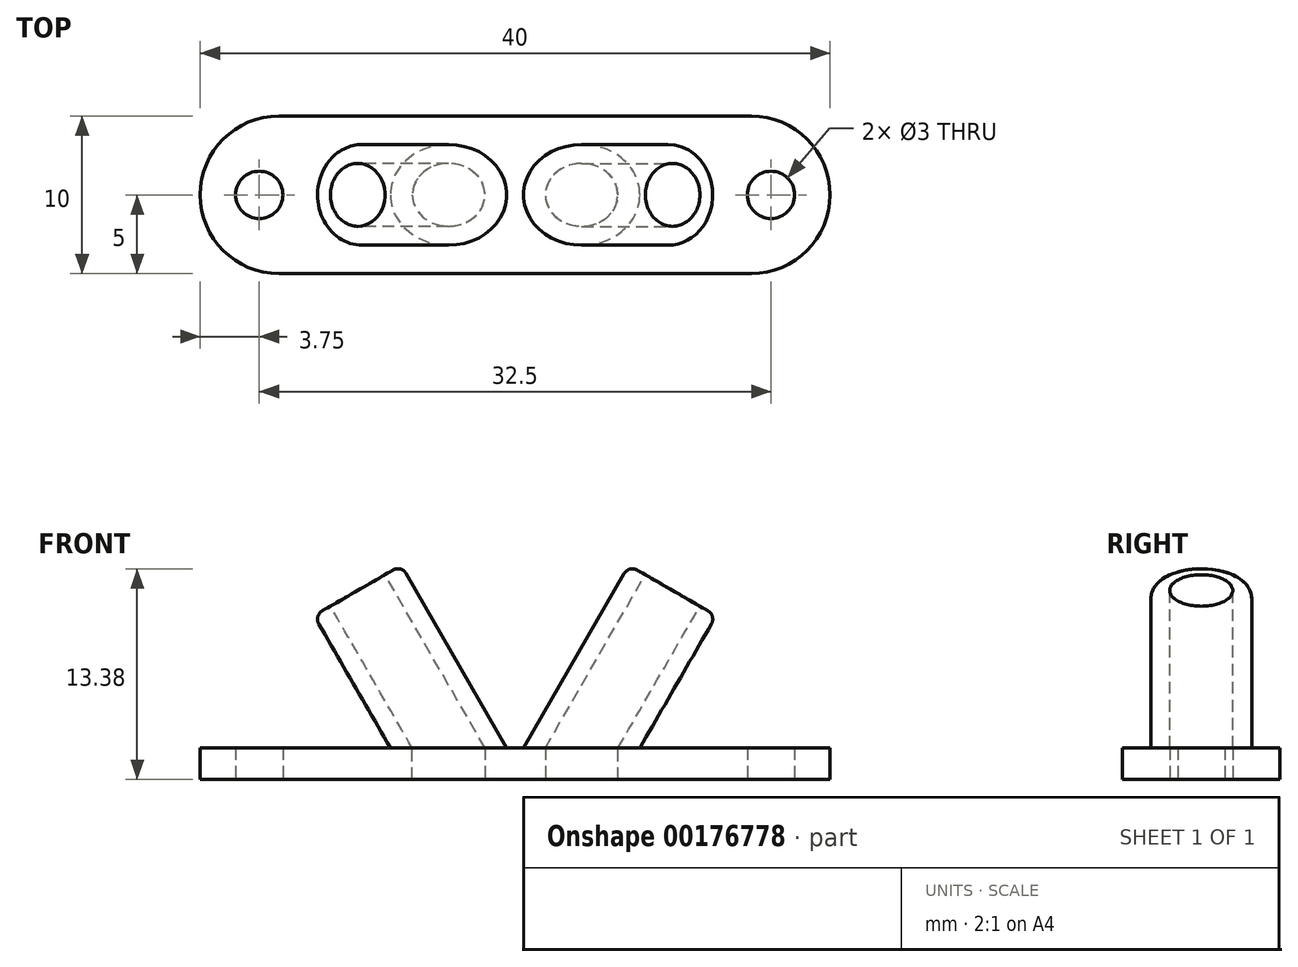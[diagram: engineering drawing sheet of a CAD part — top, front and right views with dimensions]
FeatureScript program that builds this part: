
annotation { "Feature Type Name" : "Feature", "Feature Type Description" : "" }
export const myFeature = defineFeature(function(context is Context, id is Id, definition is map)
    precondition{}
    {
        {
            var Q0;
            Q0=qCreatedBy(makeId("Top.planeOp"),FACE);
            var sketch = newSketch(context, id + "F0", { "sketchPlane" : qUnion([Q0])});
            skCircle(sketch, "E0", {"center": v(-16.25, 0) * mm, "radius": 1.5 * mm});
            skCircle(sketch, "E1.MirrorC", {"center": v(16.25, 0) * mm, "radius": 1.5 * mm});
            skLineSegment(sketch, "E2.bottom", {"start": v(-20, 5) * mm, "end": v(20, 5) * mm});
            skLineSegment(sketch, "E2.top", {"start": v(-20, -5) * mm, "end": v(20, -5) * mm});
            skLineSegment(sketch, "E2.left", {"start": v(-20, 5) * mm, "end": v(-20, -5) * mm});
            skLineSegment(sketch, "E2.right", {"start": v(20, 5) * mm, "end": v(20, -5) * mm});
            skPoint(sketch, "E2.middle", {"position": v(0, 0) * mm});
            skSolve(sketch);
        }
        {
            var Q0;
            Q0 = qSketchRegion(id + "F0", true);
            extrude(context, id + "F1", {"entities" : qUnion([Q0]), "depth" : 2 * mm});
        }
        {
            var Q0;
            Q0=makeQuery(id+"F1.opExtrude","CAP_FACE",FACE,{"disambiguationData":[OSD([sQuery(id+"F0.wireOp",EDGE,"E0"),sQuery(id+"F0.wireOp",EDGE,"E1.MirrorC"),sQuery(id+"F0.wireOp",EDGE,"E2.bottom"),sQuery(id+"F0.wireOp",EDGE,"E2.top"),sQuery(id+"F0.wireOp",EDGE,"E2.left"),sQuery(id+"F0.wireOp",EDGE,"E2.right")])],"isStart":false});
            cPlane(context, id + "F2", {"entities" : qUnion([Q0]), "cplaneType" : CPlaneType.OFFSET, "offset" : 10 * mm, "width" : 150 * mm, "height" : 150 * mm});
        }
        {
            var Q0;
            Q0=qCreatedBy(id+"F2.planeOp",FACE);
            var sketch = newSketch(context, id + "F3", { "sketchPlane" : qUnion([Q0])});
            skLineSegment(sketch, "E3.bottom", {"start": v(-10, 4.79) * mm, "end": v(10, 4.79) * mm});
            skLineSegment(sketch, "E3.top", {"start": v(-10, -4.79) * mm, "end": v(10, -4.79) * mm});
            skLineSegment(sketch, "E3.left", {"start": v(-10, 4.79) * mm, "end": v(-10, -4.79) * mm});
            skLineSegment(sketch, "E3.right", {"start": v(10, 4.79) * mm, "end": v(10, -4.79) * mm});
            skPoint(sketch, "E3.middle", {"position": v(0, 0) * mm});
            skSolve(sketch);
        }
        {
            assignVariable(context, id + "F4", {"name" : "antennaAngle", "anyValue" : 30});
        }
        {
            var Q0;
            Q0=sQuery(id+"F3.wireOp",EDGE,"E3.right");
            cPlane(context, id + "F5", {"entities" : qUnion([Q0]), "cplaneType" : CPlaneType.LINE_ANGLE, "offset" : 25 * mm, "angle" : (360 - getVariable(context, 'antennaAngle')) * degree, "width" : 150 * mm, "height" : 150 * mm});
        }
        {
            var Q0;
            Q0=sQuery(id+"F3.wireOp",EDGE,"E3.left");
            cPlane(context, id + "F6", {"entities" : qUnion([Q0]), "cplaneType" : CPlaneType.LINE_ANGLE, "offset" : 25 * mm, "angle" : (getVariable(context, 'antennaAngle')) * degree, "width" : 150 * mm, "height" : 150 * mm});
        }
        {
            var Q0;
            Q0=qCreatedBy(id+"F5.planeOp",FACE);
            var sketch = newSketch(context, id + "F7", { "sketchPlane" : qUnion([Q0])});
            skCircle(sketch, "E4", {"center": v(2.66, 0) * mm, "radius": 2 * mm});
            skCircle(sketch, "E5", {"center": v(2.66, 0) * mm, "radius": 3.2 * mm});
            skSolve(sketch);
        }
        {
            var Q0;
            Q0=makeQuery(id+"F7.imprint","IMPRINT",FACE,{"disambiguationData":[TD([[makeQuery(id+"F7.imprint","IMPRINT",EDGE,{"derivedFrom":sQuery(id+"F7.wireOp",EDGE,"E4")}),-1.0]])]});
            var Q1;
            Q1=makeQuery(id+"F1.opExtrude","CAP_FACE",FACE,{"disambiguationData":[OSD([sQuery(id+"F0.wireOp",EDGE,"E0"),sQuery(id+"F0.wireOp",EDGE,"E1.MirrorC"),sQuery(id+"F0.wireOp",EDGE,"E2.bottom"),sQuery(id+"F0.wireOp",EDGE,"E2.top"),sQuery(id+"F0.wireOp",EDGE,"E2.left"),sQuery(id+"F0.wireOp",EDGE,"E2.right")])],"isStart":false});
            extrude(context, id + "F8", {"entities" : qUnion([Q0]), "operationType" : NewBodyOperationType.ADD, "endBound" : BoundingType.UP_TO_SURFACE, "endBoundEntityFace" : qUnion([Q1]), "depth" : 25 * mm});
        }
        {
            var Q0;
            Q0=qCreatedBy(id+"F6.planeOp",FACE);
            var sketch = newSketch(context, id + "F9", { "sketchPlane" : qUnion([Q0])});
            skCircle(sketch, "E6", {"center": v(-2.66, 0) * mm, "radius": 3.2 * mm});
            skCircle(sketch, "E7", {"center": v(-2.66, 0) * mm, "radius": 2 * mm});
            skSolve(sketch);
        }
        {
            var Q0;
            Q0=makeQuery(id+"F9.imprint","IMPRINT",FACE,{"disambiguationData":[TD([[makeQuery(id+"F9.imprint","IMPRINT",EDGE,{"derivedFrom":sQuery(id+"F9.wireOp",EDGE,"E6")}),1.0]])]});
            var Q1;
            {var subQ0=sQuery(id+"F0.wireOp",EDGE,"E2.top");var subQ1=sQuery(id+"F0.wireOp",EDGE,"E2.bottom");var subQ2=sQuery(id+"F0.wireOp",EDGE,"E1.MirrorC");var subQ3=sQuery(id+"F0.wireOp",EDGE,"E0");var subQ4=sQuery(id+"F0.wireOp",EDGE,"E2.left");var subQ5=sQuery(id+"F0.wireOp",EDGE,"E2.right");Q1=makeQuery(id+"F8.boolean.opBoolean","SPLIT",FACE,{"disambiguationData":[TD([makeQuery(id+"F1.opExtrude","SWEPT_FACE",FACE,{"disambiguationData":[OSD([subQ3])]})])],"derivedFrom":makeQuery(id+"F1.opExtrude","CAP_FACE",FACE,{"disambiguationData":[OSD([subQ3,subQ2,subQ1,subQ0,subQ4,subQ5])],"isStart":false})});}
            extrude(context, id + "F10", {"entities" : qUnion([Q0]), "operationType" : NewBodyOperationType.ADD, "endBound" : BoundingType.UP_TO_SURFACE, "endBoundEntityFace" : qUnion([Q1]), "depth" : 25 * mm});
        }
        {
            var Q0;
            Q0=makeQuery(id+"F1.opExtrude","SWEPT_EDGE",EDGE,{"disambiguationData":[OSD([sQuery(id+"F0.wireOp",EDGE,"E2.top"),sQuery(id+"F0.wireOp",EDGE,"E2.left")])]});
            var Q1;
            Q1=makeQuery(id+"F1.opExtrude","SWEPT_EDGE",EDGE,{"disambiguationData":[OSD([sQuery(id+"F0.wireOp",EDGE,"E2.top"),sQuery(id+"F0.wireOp",EDGE,"E2.right")])]});
            var Q2;
            Q2=makeQuery(id+"F1.opExtrude","SWEPT_EDGE",EDGE,{"disambiguationData":[OSD([sQuery(id+"F0.wireOp",EDGE,"E2.bottom"),sQuery(id+"F0.wireOp",EDGE,"E2.right")])]});
            var Q3;
            Q3=makeQuery(id+"F1.opExtrude","SWEPT_EDGE",EDGE,{"disambiguationData":[OSD([sQuery(id+"F0.wireOp",EDGE,"E2.bottom"),sQuery(id+"F0.wireOp",EDGE,"E2.left")])]});
            fillet(context, id + "F11", {"entities" : qUnion([Q0, Q1, Q2, Q3]), "radius" : 5 * mm, "tangentPropagation" : true, "allowEdgeOverflow" : false});
        }
        {
            var Q0;
            {var subQ0=sQuery(id+"F0.wireOp",EDGE,"E2.top");var subQ1=sQuery(id+"F0.wireOp",EDGE,"E2.bottom");var subQ2=sQuery(id+"F0.wireOp",EDGE,"E1.MirrorC");var subQ3=sQuery(id+"F0.wireOp",EDGE,"E0");var subQ4=sQuery(id+"F0.wireOp",EDGE,"E2.left");var subQ5=sQuery(id+"F0.wireOp",EDGE,"E2.right");Q0=makeQuery(id+"F10.boolean.opBoolean","SPLIT",FACE,{"disambiguationData":[TD([makeQuery(id+"F10.opExtrude","SWEPT_FACE",FACE,{"disambiguationData":[OSD([sQuery(id+"F9.wireOp",EDGE,"E7")])]})])],"derivedFrom":makeQuery(id+"F8.boolean.opBoolean","SPLIT",FACE,{"disambiguationData":[TD([makeQuery(id+"F1.opExtrude","SWEPT_FACE",FACE,{"disambiguationData":[OSD([subQ3])]})])],"derivedFrom":makeQuery(id+"F1.opExtrude","CAP_FACE",FACE,{"disambiguationData":[OSD([subQ3,subQ2,subQ1,subQ0,subQ4,subQ5])],"isStart":false})})});}
            extrude(context, id + "F12", {"entities" : qUnion([Q0]), "operationType" : NewBodyOperationType.REMOVE, "endBound" : BoundingType.THROUGH_ALL, "oppositeDirection" : true, "depth" : 25 * mm});
        }
        {
            var Q0;
            Q0=makeQuery(id+"F8.boolean.opBoolean","SPLIT",FACE,{"disambiguationData":[TD([makeQuery(id+"F8.opExtrude","SWEPT_FACE",FACE,{"disambiguationData":[OSD([sQuery(id+"F7.wireOp",EDGE,"E4")])]})])],"derivedFrom":makeQuery(id+"F1.opExtrude","CAP_FACE",FACE,{"disambiguationData":[OSD([sQuery(id+"F0.wireOp",EDGE,"E0"),sQuery(id+"F0.wireOp",EDGE,"E1.MirrorC"),sQuery(id+"F0.wireOp",EDGE,"E2.bottom"),sQuery(id+"F0.wireOp",EDGE,"E2.top"),sQuery(id+"F0.wireOp",EDGE,"E2.left"),sQuery(id+"F0.wireOp",EDGE,"E2.right")])],"isStart":false})});
            extrude(context, id + "F13", {"entities" : qUnion([Q0]), "operationType" : NewBodyOperationType.REMOVE, "endBound" : BoundingType.THROUGH_ALL, "oppositeDirection" : true, "depth" : 25 * mm});
        }
        {
            var Q0;
            Q0=makeQuery(id+"F10.opExtrude","CAP_EDGE",EDGE,{"disambiguationData":[OSD([sQuery(id+"F9.wireOp",EDGE,"E6")])],"isStart":true});
            var Q1;
            Q1=makeQuery(id+"F8.opExtrude","CAP_EDGE",EDGE,{"disambiguationData":[OSD([sQuery(id+"F7.wireOp",EDGE,"E5")])],"isStart":true});
            fillet(context, id + "F14", {"entities" : qUnion([Q0, Q1]), "radius" : 0.6 * mm, "tangentPropagation" : true, "allowEdgeOverflow" : false});
        }
    });
